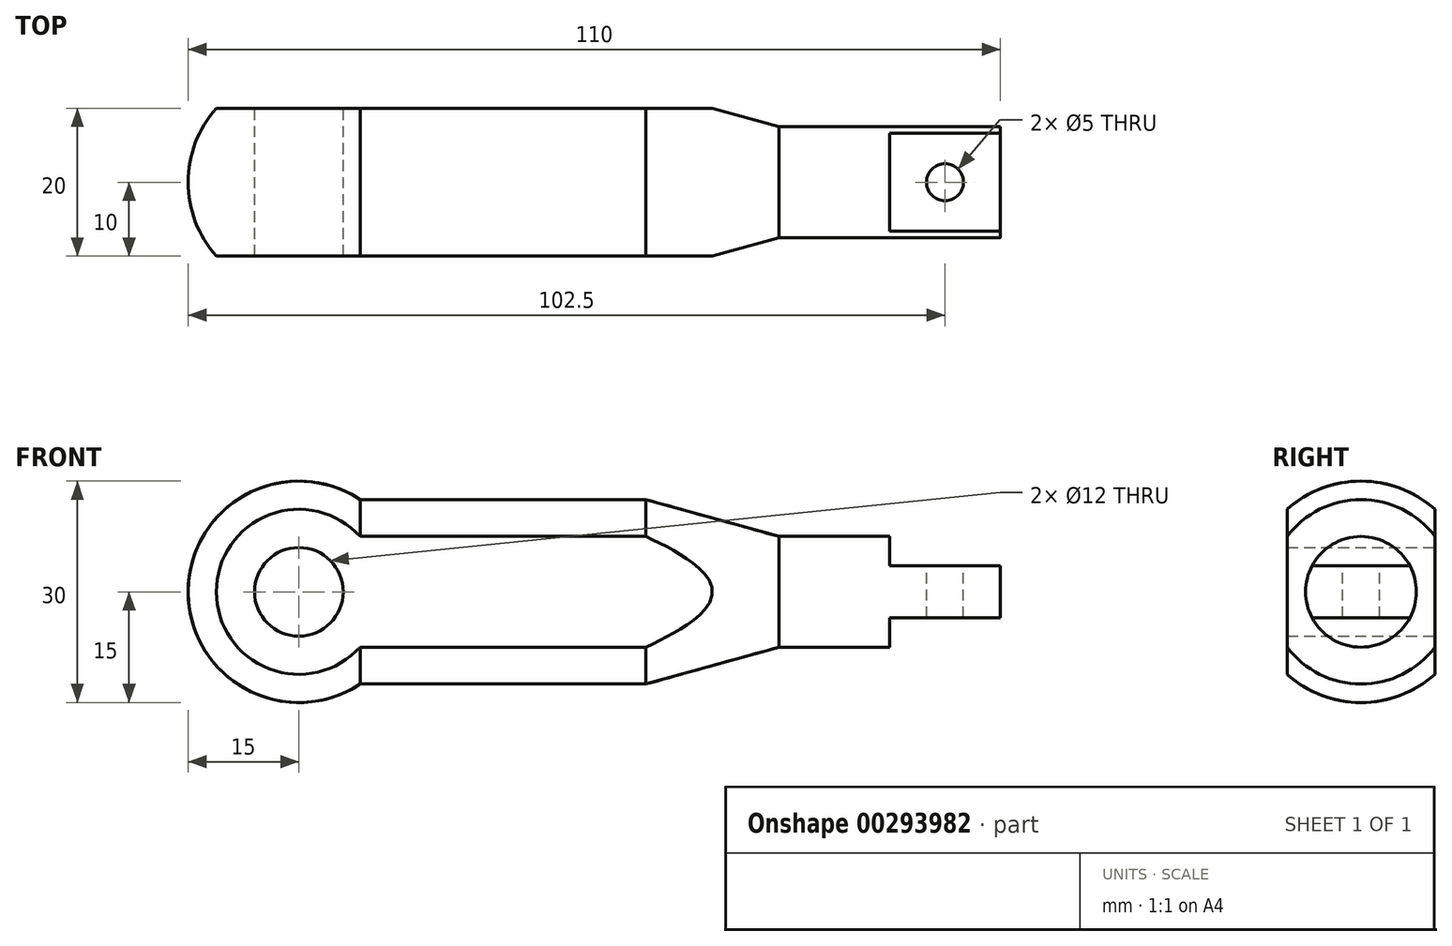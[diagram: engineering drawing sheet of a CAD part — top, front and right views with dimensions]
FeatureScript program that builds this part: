
annotation { "Feature Type Name" : "Feature", "Feature Type Description" : "" }
export const myFeature = defineFeature(function(context is Context, id is Id, definition is map)
    precondition{}
    {
        {
            var Q0;
            Q0=qCreatedBy(makeId("Front.planeOp"),FACE);
            var sketch = newSketch(context, id + "F0", { "sketchPlane" : qUnion([Q0])});
            skLineSegment(sketch, "E0", {"start": v(8.3, 12.5) * mm, "end": v(47, 12.5) * mm});
            skLineSegment(sketch, "E1", {"start": v(47, 12.5) * mm, "end": v(65, 7.5) * mm});
            skLineSegment(sketch, "E2", {"start": v(65, 7.5) * mm, "end": v(80, 7.5) * mm});
            skLineSegment(sketch, "E3", {"start": v(80, 7.5) * mm, "end": v(80, 7.5) * mm});
            skLineSegment(sketch, "E4", {"start": v(80, 7.5) * mm, "end": v(95, 7.5) * mm});
            skLineSegment(sketch, "E5", {"start": v(95, 7.5) * mm, "end": v(95, 0) * mm});
            skLineSegment(sketch, "E6", {"start": v(95, 0) * mm, "end": v(-15, 0) * mm});
            skArc(sketch, "E7", {"start": v(8.3, 12.5) * mm, "mid": v(-7.1, 13.22) * mm, "end": v(-15, 0) * mm});
            skLineSegment(sketch, "E8", {"start": v(-17.6, 0) * mm, "end": v(101.95, 0) * mm, "construction": true});
            skSolve(sketch);
        }
        {
            var Q0;
            Q0=makeQuery(id+"F0.imprint","IMPRINT",FACE,{"disambiguationData":[TD([[makeQuery(id+"F0.imprint","IMPRINT",EDGE,{"derivedFrom":sQuery(id+"F0.wireOp",EDGE,"E0")}),-1.0]])]});
            var Q1;
            Q1=sQuery(id+"F0.wireOp",EDGE,"E8");
            revolve(context, id + "F1", {"entities" : qUnion([Q0]), "axis" : qUnion([Q1]), "revolveType" : RevolveType.FULL});
        }
        {
            var Q0;
            Q0=makeQuery(id+"F1.opRevolve","SWEPT_BODY",BODY,{"disambiguationData":[OSD([sQuery(id+"F0.wireOp",EDGE,"E0"),sQuery(id+"F0.wireOp",EDGE,"E1"),sQuery(id+"F0.wireOp",EDGE,"E2"),sQuery(id+"F0.wireOp",EDGE,"E3"),sQuery(id+"F0.wireOp",EDGE,"E4"),sQuery(id+"F0.wireOp",EDGE,"E5"),sQuery(id+"F0.wireOp",EDGE,"E6"),sQuery(id+"F0.wireOp",EDGE,"E7")])]});
            var Q1;
            Q1=qCreatedBy(makeId("Top.planeOp"),FACE);
            mirror(context, id + "F2", {"entities" : qUnion([Q0]), "mirrorPlane" : qUnion([Q1])});
        }
        {
            var Q0;
            Q0=qCreatedBy(makeId("Front.planeOp"),FACE);
            var sketch = newSketch(context, id + "F3", { "sketchPlane" : qUnion([Q0])});
            skCircle(sketch, "E9", {"center": v(0, 0) * mm, "radius": 6 * mm});
            skLineSegment(sketch, "E10.bottom", {"start": v(80, 7.5) * mm, "end": v(95, 7.5) * mm});
            skLineSegment(sketch, "E10.top", {"start": v(80, 3.5) * mm, "end": v(95, 3.5) * mm});
            skLineSegment(sketch, "E10.left", {"start": v(80, 7.5) * mm, "end": v(80, 3.5) * mm});
            skLineSegment(sketch, "E10.right", {"start": v(95, 7.5) * mm, "end": v(95, 3.5) * mm});
            skLineSegment(sketch, "E11.bottom", {"start": v(80, -3.5) * mm, "end": v(95, -3.5) * mm});
            skLineSegment(sketch, "E11.top", {"start": v(80, -7.5) * mm, "end": v(95, -7.5) * mm});
            skLineSegment(sketch, "E11.left", {"start": v(80, -3.5) * mm, "end": v(80, -7.5) * mm});
            skLineSegment(sketch, "E11.right", {"start": v(95, -3.5) * mm, "end": v(95, -7.5) * mm});
            skSolve(sketch);
        }
        {
            var Q0;
            Q0 = qSketchRegion(id + "F3", true);
            extrude(context, id + "F4", {"entities" : qUnion([Q0]), "operationType" : NewBodyOperationType.REMOVE, "endBound" : BoundingType.SYMMETRIC, "depth" : 50 * mm});
        }
        {
            var Q0;
            Q0=qCreatedBy(makeId("Top.planeOp"),FACE);
            var sketch = newSketch(context, id + "F5", { "sketchPlane" : qUnion([Q0])});
            skCircle(sketch, "E12", {"center": v(87.5, 0) * mm, "radius": 2.5 * mm});
            skLineSegment(sketch, "E13.bottom", {"start": v(-15.98, 16.06) * mm, "end": v(67.65, 16.06) * mm});
            skLineSegment(sketch, "E13.top", {"start": v(-15.98, 10) * mm, "end": v(67.65, 10) * mm});
            skLineSegment(sketch, "E13.left", {"start": v(-15.98, 16.06) * mm, "end": v(-15.98, 10) * mm});
            skLineSegment(sketch, "E13.right", {"start": v(67.65, 16.06) * mm, "end": v(67.65, 10) * mm});
            skLineSegment(sketch, "E14.bottom", {"start": v(-16.24, -10) * mm, "end": v(67.65, -10) * mm});
            skLineSegment(sketch, "E14.top", {"start": v(-16.24, -18.14) * mm, "end": v(67.65, -18.14) * mm});
            skLineSegment(sketch, "E14.left", {"start": v(-16.24, -10) * mm, "end": v(-16.24, -18.14) * mm});
            skLineSegment(sketch, "E14.right", {"start": v(67.65, -10) * mm, "end": v(67.65, -18.14) * mm});
            skSolve(sketch);
        }
        {
            var Q0;
            Q0 = qSketchRegion(id + "F5", true);
            extrude(context, id + "F6", {"entities" : qUnion([Q0]), "operationType" : NewBodyOperationType.REMOVE, "endBound" : BoundingType.SYMMETRIC, "oppositeDirection" : true, "depth" : 50 * mm});
        }
    });
